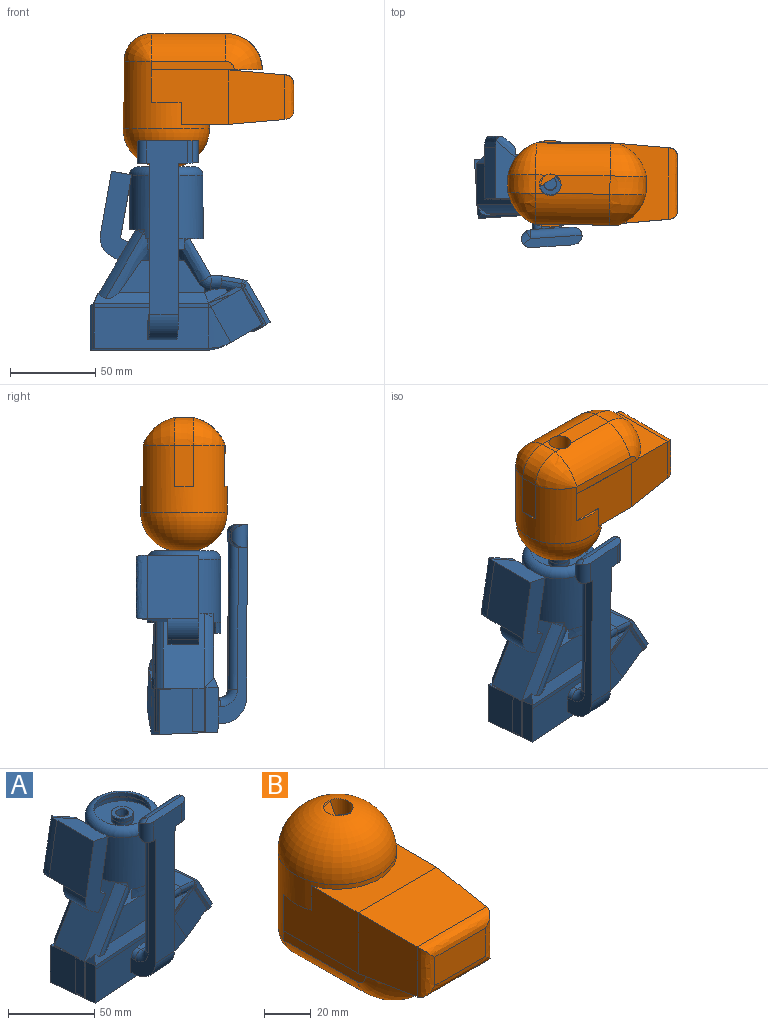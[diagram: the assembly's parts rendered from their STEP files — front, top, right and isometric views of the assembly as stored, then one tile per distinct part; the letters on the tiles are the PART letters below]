
ASSEMBLY  parts=2 mates=1
PART A: 203 faces, bbox 112.8x73.1x126.7 mm
  f0: cylinder r=21.59mm len=43.18mm, axis (0,0,-1), area 4752.9mm2, adj f1,f2,f171,f172,f173,f174,f175,f176
  f1: revolved ~3.1x1.99mm, area 1.9mm2, adj f0,f2,f189
  f2: torus R=17.89mm, axis (0,-1,0), area 8.5mm2, adj f0,f1,f3
  f3: cylinder r=21.59mm len=46.42mm, axis (0.5,0,0.87), area 346.5mm2, adj f2,f4,f155,f156,f170,f189
  f4: plane 34.51x27.74mm, normal (-1,-0.06,0), area 712.3mm2, adj f3,f5,f111,f112,f142,f143,f151,f152
  f5: plane 8.3x6.75mm, normal (-0.94,-0.05,0.34), area 24.2mm2, adj f4,f6,f170
  f6: plane 67.23x6.83mm, normal (0.06,-0.92,0.38), area 407.3mm2, adj f5,f7,f109,f110,f111,f170,f189
  f7: plane 13.56x8.49mm, normal (-0.05,-0.94,0.34), area 67.2mm2, adj f6,f8,f103,f106,f107,f108
  f8: plane 16.43x9.52mm, normal (-0.5,0,0.87), area 14.9mm2, adj f7,f9,f107,f108
  f9: plane 19.5x11.72mm, normal (0.09,-1,0), area 49.8mm2, adj f8,f10,f11,f12,f13,f100,f101,f102
  f10: plane 11.9x4.35mm, normal (0.34,-0.01,-0.94), area 0.6mm2, adj f9,f11,f12
  f11: plane 0.23x0.1mm, normal (0.94,0.07,0.34), area 0mm2, adj f9,f10,f12
  f12: plane 11.9x4.58mm, normal (-0.05,-0.94,0.34), area 1.7mm2, adj f9,f10,f11
  f13: extruded ~3.02x2.86mm, area 2.2mm2, adj f9,f14,f98,f99,f100,f107
  f14: extruded ~3.31x3.22mm, area 4.2mm2, adj f13,f15,f97,f98,f99,f107
  f15: plane 34.5x5.38mm, normal (0.34,0.03,0.94), area 88.3mm2, adj f14,f16,f93,f94,f95,f97
  f16: extruded ~0.48x0.2mm, area 0mm2, adj f15,f17,f93
  f17: extruded ~12.55x2.7mm, area 6.3mm2, adj f16,f18,f91,f95
  f18: extruded ~13.22x11.37mm, area 105.1mm2, adj f17,f19,f88,f89,f90,f91
  f19: plane 19.3x12.22mm, normal (-0.34,0.01,0.94), area 94.5mm2, adj f18,f20,f84,f85,f86,f87,f90,f91
  f20: revolved ~13.69x10.91mm, area 48mm2, adj f19,f21,f83,f85,f86,f91
  f21: extruded ~27.45x20.95mm, area 271.7mm2, adj f20,f22,f54,f81,f82,f178,f179
  f22: extruded ~10.52x5.36mm, area 20.8mm2, adj f21,f23,f54,f83
  f23: plane 46.38x20.02mm, normal (-0.06,1,-0.04), area 730.9mm2, adj f22,f24,f53,f54,f83,f86
  f24: plane 45.53x4.73mm, normal (0,-0.04,-1), area 80.9mm2, adj f23,f25,f53,f86
  f25: plane 52.9x6.46mm, normal (-0.06,0.95,0.31), area 332.6mm2, adj f24,f26,f27,f87,f177
  f26: bspline ~12.27x6.84mm, area 0.1mm2, adj f25,f177
  f27: plane 53.47x3.48mm, normal (-0.06,1,0.01), area 55.7mm2, adj f25,f28,f143,f177
  f28: cone r=1.04mm half-angle=87.5deg, axis (-0.06,1,-0.04), area 0.3mm2, adj f27,f29,f52
  f29: cone r=26.42mm half-angle=87.5deg, axis (-0.06,1,-0.04), area 182.6mm2, adj f28,f30,f50,f143
  f30: plane 34.58x34.37mm, normal (-0.09,1,0), area 639.3mm2, adj f29,f31,f49,f52
  f31: plane 36.34x21.82mm, normal (0.5,0,-0.87), area 603.9mm2, adj f30,f32,f40,f41,f42,f43,f44,f45
  f32: extruded ~23.51x15.37mm, area 39.8mm2, adj f31,f33,f34,f40,f41,f48
  f33: extruded ~1.32x1.25mm, area 0.1mm2, adj f32,f40,f41
  f34: plane 35.15x11.09mm, normal (0.5,0.04,-0.87), area 298.9mm2, adj f32,f35,f38,f41,f42,f43,f44,f45
  f35: extruded ~22.07x12.78mm, area 3.8mm2, adj f34,f36,f38,f49
  f36: extruded ~1.91x1.19mm, area 0.3mm2, adj f35,f37,f38,f88
  f37: extruded ~3.94x3.67mm, area 2.6mm2, adj f36,f49,f52,f88,f89
  f38: extruded ~24.45x14.35mm, area 13.9mm2, adj f34,f35,f36,f39,f88,f93,f94
  f39: extruded ~0.23x0.22mm, area 0mm2, adj f38,f88,f93
  f40: plane 20.7x11.99mm, normal (0.09,-1,0), area 2.3mm2, adj f31,f32,f33,f41
  f41: extruded ~26.12x21.03mm, area 54.4mm2, adj f31,f32,f33,f34,f40,f42
  f42: extruded ~7.46x3.13mm, area 7.5mm2, adj f31,f34,f41,f43
  f43: extruded ~12.43x5.79mm, area 4mm2, adj f31,f34,f42,f44
  f44: extruded ~2.59x2.28mm, area 0.3mm2, adj f31,f34,f43,f45
  f45: extruded ~0.5x0.45mm, area 0.1mm2, adj f31,f34,f44,f46
  f46: extruded ~4.69x3.89mm, area 0.4mm2, adj f31,f34,f45
  f47: extruded ~23.89x16.07mm, area 59.1mm2, adj f31,f34,f48,f99,f100,f101
  f48: extruded ~1.59x1.31mm, area 1mm2, adj f31,f32,f34,f47
  f49: extruded ~22.17x12.95mm, area 8.9mm2, adj f30,f34,f35,f37
  f50: cylinder r=26.42mm len=35.34mm, axis (0.06,-1,0.04), area 476.5mm2, adj f29,f31,f51,f142
  f51: cone r=2.54mm half-angle=87.5deg, axis (-0.06,1,-0.04), area 181.2mm2, adj f50,f101,f102,f112
  f52: plane 22.23x13.49mm, normal (-0.09,1,0), area 26.3mm2, adj f28,f30,f37,f89
  f53: extruded ~19.11x9.91mm, area 38.1mm2, adj f23,f24,f54,f177
  f54: plane 36.89x32.62mm, normal (0,0.04,1), area 665mm2, adj f21,f22,f23,f53,f55,f81,f110,f177
  f55: cylinder r=3.81mm len=11.62mm, axis (0.5,0,0.87), area 102.6mm2, adj f54,f56,f177,f189
  f56: torus R=17.89mm, axis (0,-1,0), area 66.4mm2, adj f55,f57,f67,f70
  f57: revolved ~14.19x10.25mm, area 124.6mm2, adj f56,f58,f189
  f58: extruded ~14.19x10.18mm, area 100mm2, adj f57,f59,f70,f187,f188,f189
  f59: bspline ~13.51x6.46mm, area 97.1mm2, adj f58,f60,f65,f66
  f60: cone r=3.81mm half-angle=1deg, axis (0,0,1), area 16.8mm2, adj f59,f61,f65,f70
  f61: bspline ~13.67x7.63mm, area 101.2mm2, adj f60,f62,f63,f65
  f62: plane 6.35x2.48mm, normal (0.61,0.79,0.02), area 18.9mm2, adj f61,f65,f185,f186
  f63: revolved ~14x12.32mm, area 80.8mm2, adj f61,f64,f184,f185
  f64: torus R=12.08mm, axis (-0.09,1,0), area 50.2mm2, adj f63,f70,f81,f82
  f65: plane 23.82x20.6mm, normal (0,0,-1), area 171.6mm2, adj f59,f60,f61,f62,f66,f186
  f66: plane 6.35x2.91mm, normal (-0.59,0.81,0.02), area 21.8mm2, adj f59,f65,f186,f187
  f67: revolved ~13.89x10.22mm, area 122mm2, adj f56,f68,f177
  f68: extruded ~13.89x10.15mm, area 98.4mm2, adj f67,f69,f70,f177,f178
  f69: extruded ~1.07x0.25mm, area 0.3mm2, adj f68,f177,f178
  f70: cylinder r=3.81mm len=34.54mm, axis (0,0,1), area 778.7mm2, adj f56,f58,f60,f64,f68,f71,f178
  f71: plane 7.62x7.62mm, normal (0,0,-1), area 6.2mm2, adj f70,f72
  f72: cone r=3.81mm half-angle=3deg, axis (0,0,1), area 117.4mm2, adj f71,f73
  f73: plane 12.7x12.7mm, normal (0,0,1), area 81.2mm2, adj f72,f74
  f74: cone r=6.35mm half-angle=3deg, axis (0,0,1), area 100.4mm2, adj f73,f75
  f75: plane 12.7x12.7mm, normal (0,0,1), area 5.3mm2, adj f74,f76
  f76: cylinder r=6.35mm len=12.7mm, axis (0,0,1), area 101.3mm2, adj f75,f77
  f77: plane 38.1x38.1mm, normal (0,0,1), area 1013.4mm2, adj f76,f78
  f78: cylinder r=19.05mm len=38.1mm, axis (0,0,-1), area 304mm2, adj f77,f79
  f79: torus R=16.51mm, axis (0,0,1), area 454.4mm2, adj f78,f80
  f80: cylinder r=16.51mm len=33.02mm, axis (0,0,1), area 263.5mm2, adj f79,f171
  f81: cylinder r=3.81mm len=9.74mm, axis (-0.5,-0.04,0.87), area 92.3mm2, adj f21,f54,f64,f184
  f82: revolved ~13.78x9.31mm, area 41.7mm2, adj f21,f64,f178
  f83: extruded ~1.8x1.62mm, area 3.6mm2, adj f20,f22,f23,f86
  f84: cylinder r=3.81mm len=5.38mm, axis (-1,-0.09,0), area 10.4mm2, adj f19,f85
  f85: torus R=12.08mm, axis (-0.09,1,0), area 26.5mm2, adj f19,f20,f84,f86
  f86: plane 20.13x7.11mm, normal (1,0.06,0), area 57.2mm2, adj f19,f20,f23,f24,f83,f85
  f87: plane 13.35x10.78mm, normal (-0.17,0.95,0.27), area 75.7mm2, adj f19,f25,f89,f90
  f88: extruded ~4.86x3.64mm, area 6mm2, adj f18,f36,f37,f38,f39,f89,f93
  f89: plane 22.51x13.38mm, normal (-0.5,0,0.87), area 45.6mm2, adj f18,f37,f52,f87,f88,f90
  f90: plane 8.78x4.79mm, normal (0.94,0.07,0.34), area 18.4mm2, adj f18,f19,f87,f89
  f91: extruded ~9.64x9.16mm, area 68.8mm2, adj f17,f18,f19,f20,f92
  f92: plane 34.84x9.31mm, normal (0,0,1), area 218.5mm2, adj f91,f95,f106,f179
  f93: extruded ~2.55x1.34mm, area 1.2mm2, adj f15,f16,f38,f39,f88
  f94: plane 35.5x24.2mm, normal (0.86,0.08,0.5), area 961.6mm2, adj f15,f34,f38,f99
  f95: plane 35.37x15.44mm, normal (0.17,0.02,0.98), area 437.1mm2, adj f15,f17,f92,f96
  f96: extruded ~12.86x4.73mm, area 32.3mm2, adj f95,f97,f106,f107
  f97: extruded ~2.42x0.85mm, area 0mm2, adj f14,f15,f96
  f98: revolved ~1.91x1.74mm, area 0.7mm2, adj f13,f14,f99
  f99: extruded ~25.65x16.38mm, area 82.6mm2, adj f13,f14,f34,f47,f94,f98,f100
  f100: extruded ~2.62x2.35mm, area 2.4mm2, adj f9,f13,f47,f99
  f101: plane 31.27x30.14mm, normal (0.09,-1,0), area 505.1mm2, adj f9,f31,f47,f51
  f102: cone r=0mm half-angle=87.5deg, axis (-0.06,1,-0.04), area 1.7mm2, adj f9,f51,f111
  f103: plane 6.79x6.57mm, normal (-0.34,0.01,0.94), area 10.7mm2, adj f7,f104,f105,f106
  f104: plane 6.08x3.26mm, normal (1,0.06,0), area 6mm2, adj f103,f105,f110
  f105: revolved ~10.71x10.01mm, area 57.5mm2, adj f103,f104,f106,f110,f184
  f106: extruded ~8.61x6.66mm, area 55mm2, adj f7,f92,f96,f103,f105,f107
  f107: extruded ~13.56x8.57mm, area 58.2mm2, adj f7,f8,f9,f13,f14,f96,f106,f108
  f108: plane 3.4x2.07mm, normal (0.94,0.07,0.34), area 3.3mm2, adj f7,f8,f107
  f109: bspline ~10.04x6.13mm, area 30.8mm2, adj f6,f170,f189
  f110: plane 50.31x19.34mm, normal (0.06,-1,0.04), area 719.1mm2, adj f6,f54,f104,f105,f184,f189
  f111: plane 67.17x4.39mm, normal (0.06,-1,-0.01), area 171mm2, adj f4,f6,f102,f112
  f112: plane 67.17x23.93mm, normal (0.06,-1,-0.01), area 1365.1mm2, adj f4,f51,f111,f113,f137,f138,f139,f140
  f113: plane 17.04x4.64mm, normal (0,0.01,-1), area 59.9mm2, adj f112,f114,f137,f141
  f114: cylinder r=15.14mm len=17.79mm, axis (1,0.06,0), area 400.4mm2, adj f113,f115,f137,f141
  f115: plane 101.86x23.93mm, normal (0.06,-1,-0.01), area 1809.5mm2, adj f114,f116,f133,f134,f135,f136,f137,f141
  f116: cylinder r=10.38mm len=13.14mm, axis (0,0.01,-1), area 39.1mm2, adj f115,f117,f133,f136
  f117: cylinder r=5.08mm len=13.19mm, axis (0,0.01,-1), area 149.9mm2, adj f116,f118,f131,f132,f133,f136
  f118: cylinder r=5.08mm len=30.45mm, axis (1,0.06,0), area 220.6mm2, adj f117,f119,f131,f136
  f119: sphere r=5.08mm, area 13.5mm2, adj f118,f120,f130
  f120: cylinder r=5.08mm len=7.41mm, axis (0.83,0.56,0), area 29.3mm2, adj f119,f121,f135,f136
  f121: plane 3.29x0.36mm, normal (-0.56,0.83,0), area 1.4mm2, adj f120,f122,f130,f135
  f122: cylinder r=5.08mm len=7.41mm, axis (0.83,0.56,0), area 29.3mm2, adj f121,f123,f134,f135
  f123: sphere r=5.08mm, area 8.6mm2, adj f122,f124,f130
  f124: cylinder r=5.08mm len=6.83mm, axis (-1,-0.06,0), area 26.2mm2, adj f123,f125,f131,f134
  f125: cylinder r=5.08mm len=88.44mm, axis (0,0.01,-1), area 685.2mm2, adj f124,f126,f131,f141
  f126: torus R=10.16mm, axis (-1,-0.06,0), area 86.8mm2, adj f125,f127,f140,f141
  f127: cylinder r=5.08mm len=7mm, axis (-1,-0.06,0), area 53.3mm2, adj f126,f128,f131,f139
  f128: torus R=10.16mm, axis (-1,-0.06,0), area 86.8mm2, adj f127,f129,f137,f138
  f129: cylinder r=5.08mm len=88.75mm, axis (0,-0.01,1), area 687.7mm2, adj f128,f131,f132,f137
  f130: cylinder r=5.08mm len=3.29mm, axis (0,0.01,-1), area 8.7mm2, adj f119,f121,f123,f131
  f131: plane 91.7x25.05mm, normal (-0.06,1,0.01), area 669.3mm2, adj f117,f118,f124,f125,f127,f129,f130,f132
  f132: cylinder r=5.08mm len=17.29mm, axis (1,0.06,0), area 95.1mm2, adj f117,f129,f131,f133
  f133: plane 11.9x6.06mm, normal (0,0.01,-1), area 56.5mm2, adj f115,f116,f117,f132,f137
  f134: plane 6.36x5.41mm, normal (0,0.01,-1), area 23.1mm2, adj f115,f122,f124,f135,f141
  f135: cylinder r=5.08mm len=13.5mm, axis (0,-0.01,1), area 138.3mm2, adj f115,f120,f121,f122,f134,f136
  f136: plane 34.72x7.28mm, normal (0,-0.01,1), area 168.7mm2, adj f115,f116,f117,f118,f120,f135
  f137: plane 103.8x19.26mm, normal (1,0.06,0), area 657.8mm2, adj f112,f113,f114,f115,f128,f129,f133,f138
  f138: cylinder r=5.08mm len=5.28mm, axis (0.06,-1,-0.01), area 25.8mm2, adj f112,f128,f137,f139
  f139: plane 6.88x3.66mm, normal (0,-0.01,1), area 21.6mm2, adj f112,f127,f138,f140
  f140: cylinder r=5.08mm len=5.28mm, axis (-0.06,1,0.01), area 25.8mm2, adj f112,f126,f139,f141
  f141: plane 103.49x19.26mm, normal (-1,-0.06,0), area 656.2mm2, adj f112,f113,f114,f115,f125,f126,f134,f140
  f142: plane 69.4x38.73mm, normal (0,-0.04,-1), area 2318.8mm2, adj f4,f50,f112,f143
  f143: plane 67.17x25.43mm, normal (-0.06,1,0.01), area 1484.9mm2, adj f4,f27,f29,f142,f144,f147,f148,f151
  f144: extruded ~23.41x4.19mm, area 109mm2, adj f143,f145,f147,f177
  f145: extruded ~25.4x3.18mm, area 85.2mm2, adj f144,f146,f147,f148,f177
  f146: revolved ~3.96x1.92mm, area 1.9mm2, adj f145,f177
  f147: plane 9.33x2.82mm, normal (0,0,-1), area 14.5mm2, adj f143,f144,f145,f148
  f148: extruded ~25.4x4.25mm, area 71.4mm2, adj f143,f145,f147,f149,f150,f151,f152
  f149: plane 13x0.49mm, normal (-1,0,0), area 3.2mm2, adj f148,f152,f156
  f150: cylinder r=21.59mm len=45.84mm, axis (0.5,0,0.87), area 277.6mm2, adj f148,f156,f175,f177
  f151: plane 3.35x1.04mm, normal (-0.06,1,0.01), area 3.5mm2, adj f4,f143,f148,f152
  f152: plane 21.6x3.37mm, normal (0,0.04,1), area 14.6mm2, adj f4,f148,f149,f151,f156
  f153: plane 25.4x7.15mm, normal (-1,0,0), area 179.6mm2, adj f4,f154,f155,f156
  f154: plane 7.78x0.51mm, normal (0,0,-1), area 1.8mm2, adj f4,f153,f155
  f155: extruded ~25.4x0.63mm, area 20.2mm2, adj f3,f4,f153,f154
  f156: plane 43.99x25.4mm, normal (-0.87,0,0.5), area 1007.5mm2, adj f3,f4,f149,f150,f152,f153,f157,f167
  f157: plane 52.21x18.57mm, normal (0,-1,0), area 605.4mm2, adj f156,f158,f159,f166,f167,f169,f173
  f158: cylinder r=12.04mm len=18.2mm, axis (0,-1,0), area 267.8mm2, adj f157,f159,f168,f169
  f159: plane 37.02x30.11mm, normal (-0.98,0,0.17), area 1132mm2, adj f157,f158,f160,f165,f166
  f160: plane 15.83x11.86mm, normal (-0.17,0,-0.98), area 133.4mm2, adj f159,f161,f165,f168,f173
  f161: bspline ~17.63x15.42mm, area 86.7mm2, adj f160,f162,f164,f165,f173
  f162: bspline ~41.04x8.97mm, area 140.9mm2, adj f161,f163,f164,f173
  f163: bspline ~16.75x15.42mm, area 86.6mm2, adj f162,f164,f165,f166,f173
  f164: plane 27.34x6.62mm, normal (0.63,0.77,-0.11), area 67.4mm2, adj f161,f162,f163,f165
  f165: bspline ~42.17x15.4mm, area 473.5mm2, adj f159,f160,f161,f163,f164,f166
  f166: plane 34.04x11.86mm, normal (0.17,0,0.98), area 340.4mm2, adj f157,f159,f163,f165,f171,f173
  f167: plane 18.2x4.62mm, normal (0.5,0,0.87), area 97.1mm2, adj f156,f157,f168,f173
  f168: plane 16.66x15.19mm, normal (0,1,0), area 152.8mm2, adj f156,f158,f160,f167,f169
  f169: plane 18.2x4.62mm, normal (-0.5,0,-0.87), area 97.1mm2, adj f156,f157,f158,f168
  f170: bspline ~16.34x13.78mm, area 29.2mm2, adj f3,f5,f6,f109
  f171: torus R=16.51mm, axis (0,0,1), area 981.5mm2, adj f0,f80,f166,f172,f173
  f172: torus R=16.51mm, axis (0,0,1), area 0mm2, adj f0,f171,f173
  f173: plane 37.37x28.88mm, normal (0.98,0,-0.17), area 999.2mm2, adj f0,f157,f160,f161,f162,f163,f166,f167
  f174: plane 24.16x3.7mm, normal (0,0,-1), area 60.6mm2, adj f0,f156
  f175: torus R=17.89mm, axis (0,-1,0), area 5.1mm2, adj f0,f150,f176
  f176: revolved ~2.72x2.24mm, area 2.2mm2, adj f0,f175,f177
  f177: extruded ~50.27x36.26mm, area 630mm2, adj f0,f25,f26,f27,f53,f54,f55,f67
  f178: plane 41.45x37.68mm, normal (0,0,-1), area 406.3mm2, adj f0,f21,f68,f69,f70,f82,f177,f179
  f179: plane 35.45x22.06mm, normal (0.86,0.08,0.5), area 860.9mm2, adj f0,f21,f92,f178,f180,f181,f182,f183
  f180: plane 2.84x0.57mm, normal (1,0.06,0), area 1.3mm2, adj f179,f181,f182,f183
  f181: plane 2.83x1.64mm, normal (-0.06,1,-0.04), area 2.3mm2, adj f179,f180,f182
  f182: plane 1.7x1.69mm, normal (0,0.04,1), area 1.6mm2, adj f179,f180,f181,f183
  f183: extruded ~2.87x1.57mm, area 2.8mm2, adj f179,f180,f182
  f184: extruded ~27.78x23.85mm, area 357.4mm2, adj f0,f54,f63,f81,f105,f110,f179,f185
  f185: plane 5.61x2.37mm, normal (0,0,-1), area 2.9mm2, adj f0,f62,f63,f184
  f186: cone r=21.59mm half-angle=1deg, axis (0,0,-1), area 142.5mm2, adj f0,f62,f65,f66
  f187: plane 4.46x1.97mm, normal (0,0,-1), area 2.2mm2, adj f0,f58,f66,f188
  f188: extruded ~0.65x0.25mm, area 0.2mm2, adj f0,f58,f187,f189
  f189: extruded ~46.64x33.51mm, area 468.1mm2, adj f0,f1,f3,f6,f54,f55,f57,f58
  f190: plane 7.21x3.02mm, normal (0.94,0.07,0.34), area 6mm2, adj f191,f192
  f191: cylinder r=3.81mm len=5.72mm, axis (-0.98,-0.09,0.17), area 0mm2, adj f190,f192
  f192: plane 8.82x5.03mm, normal (-0.5,0,0.87), area 8mm2, adj f190,f191
  f193: cylinder r=3.81mm len=8.17mm, axis (0.5,0,0.87), area 8mm2, adj f194,f195,f196,f197
  f194: bspline ~9.02x5.58mm, area 6.2mm2, adj f193,f195,f197
  f195: bspline ~12.49x6.84mm, area 3.2mm2, adj f193,f194,f196
  f196: extruded ~1.45x1.02mm, area 0.7mm2, adj f193,f195,f197
  f197: extruded ~1.41x0.82mm, area 0.6mm2, adj f193,f194,f196
  f198: extruded ~1.95x1.48mm, area 1.3mm2, adj f199,f200,f201
  f199: extruded ~1.9x1.08mm, area 1mm2, adj f198,f200,f202
  f200: cylinder r=3.81mm len=8.79mm, axis (0.5,0,0.87), area 13.1mm2, adj f198,f199,f201,f202
  f201: bspline ~13.47x10.2mm, area 4.6mm2, adj f198,f200,f202
  f202: bspline ~8.83x5.45mm, area 9.3mm2, adj f199,f200,f201
PART B: 33 faces, bbox 50.8x100.2x78.3 mm
  f0: torus R=2.54mm, axis (0,0,1), area 3752.5mm2, adj f4,f32
  f1: cylinder r=25.4mm len=43.94mm, axis (-0.01,1,0), area 1134.9mm2, adj f2,f23,f26,f27,f29,f32
  f2: plane 32.2x11.2mm, normal (0.01,0,-1), area 318.1mm2, adj f1,f3,f30,f32
  f3: cylinder r=25.4mm len=43.93mm, axis (-0.01,1,0), area 1102.1mm2, adj f2,f22,f27,f28,f31,f32
  f4: cylinder r=25.4mm len=50.8mm, axis (0,0,-1), area 2866.1mm2, adj f0,f5,f6,f7,f8,f9,f11,f12
  f5: plane 16.58x1.39mm, normal (0,0,-1), area 15.5mm2, adj f4,f11
  f6: plane 10.75x0.58mm, normal (0,0,-1), area 4.1mm2, adj f4,f8
  f7: plane 17.89x1.63mm, normal (0,0,-1), area 19.5mm2, adj f4,f9
  f8: plane 24.13x10.75mm, normal (0,1,0), area 259.4mm2, adj f4,f6,f24
  f9: plane 45.61x32mm, normal (1,0,0), area 1228.1mm2, adj f4,f7,f12,f13,f25
  f10: plane 44.96x0.62mm, normal (0,0,-1), area 13.9mm2, adj f11,f16,f26
  f11: plane 44.96x32mm, normal (-1,0,0), area 1224.1mm2, adj f4,f5,f10,f12,f15
  f12: plane 47.78x28.38mm, normal (0,0,1), area 756.2mm2, adj f4,f9,f11,f14
  f13: plane 32.89x32mm, normal (1,-0.09,0), area 961.8mm2, adj f9,f14,f16,f21
  f14: plane 47.78x32.89mm, normal (0,-0.09,1), area 1482.7mm2, adj f12,f13,f15,f20
  f15: plane 32.89x32mm, normal (-1,-0.09,0), area 961.8mm2, adj f11,f14,f16,f18
  f16: plane 47.78x32.89mm, normal (0,-0.09,-1), area 1482.7mm2, adj f10,f13,f15,f19,f25
  f17: plane 30.66x14.89mm, normal (0,-1,0), area 456.5mm2, adj f18,f19,f20,f21
  f18: bspline ~28.87x5.68mm, area 178.8mm2, adj f15,f17,f19,f20
  f19: bspline ~46.23x5.68mm, area 315.9mm2, adj f16,f17,f18,f21
  f20: bspline ~46.23x5.68mm, area 315.9mm2, adj f14,f17,f18,f21
  f21: bspline ~28.87x5.68mm, area 178.8mm2, adj f13,f17,f19,f20
  f22: revolved ~18.4x16.13mm, area 382.1mm2, adj f3,f4,f24
  f23: revolved ~18.86x16.54mm, area 400.1mm2, adj f1,f4,f24
  f24: cone r=16.28mm half-angle=0.8deg, axis (-1,-0.01,0), area 273.6mm2, adj f8,f22,f23,f27
  f25: plane 65.44x47.83mm, normal (0,0,1), area 760.5mm2, adj f9,f16,f26,f28,f29,f30,f31
  f26: plane 48.76x5.08mm, normal (-1,-0.01,0), area 242.2mm2, adj f1,f4,f10,f25,f29
  f27: plane 10.83x5.92mm, normal (0.01,0,-1), area 34mm2, adj f1,f3,f24,f32
  f28: plane 48.76x5.08mm, normal (1,0.01,0), area 242.2mm2, adj f3,f4,f25,f31
  f29: revolved ~21.36x21.36mm, area 607.8mm2, adj f1,f25,f26,f30
  f30: cone r=21.36mm half-angle=0.8deg, axis (-1,-0.01,0), area 359.4mm2, adj f2,f25,f29,f31
  f31: revolved ~21.46x21.21mm, area 584.5mm2, adj f3,f25,f28,f30
  f32: cylinder r=6.35mm len=78.27mm, axis (0,0,1), area 3114.4mm2, adj f0,f1,f2,f3,f27
PLACE A t=(-46.49,24.58,-19.7)mm
PLACE B rot(axis=(0.71,-0.71,0),180deg) t=(11,-56.45,46.15)mm
MATE ball B.f0 <-> A.f0  axis (0,0,-1) through (11,-10.4,8.24)mm
